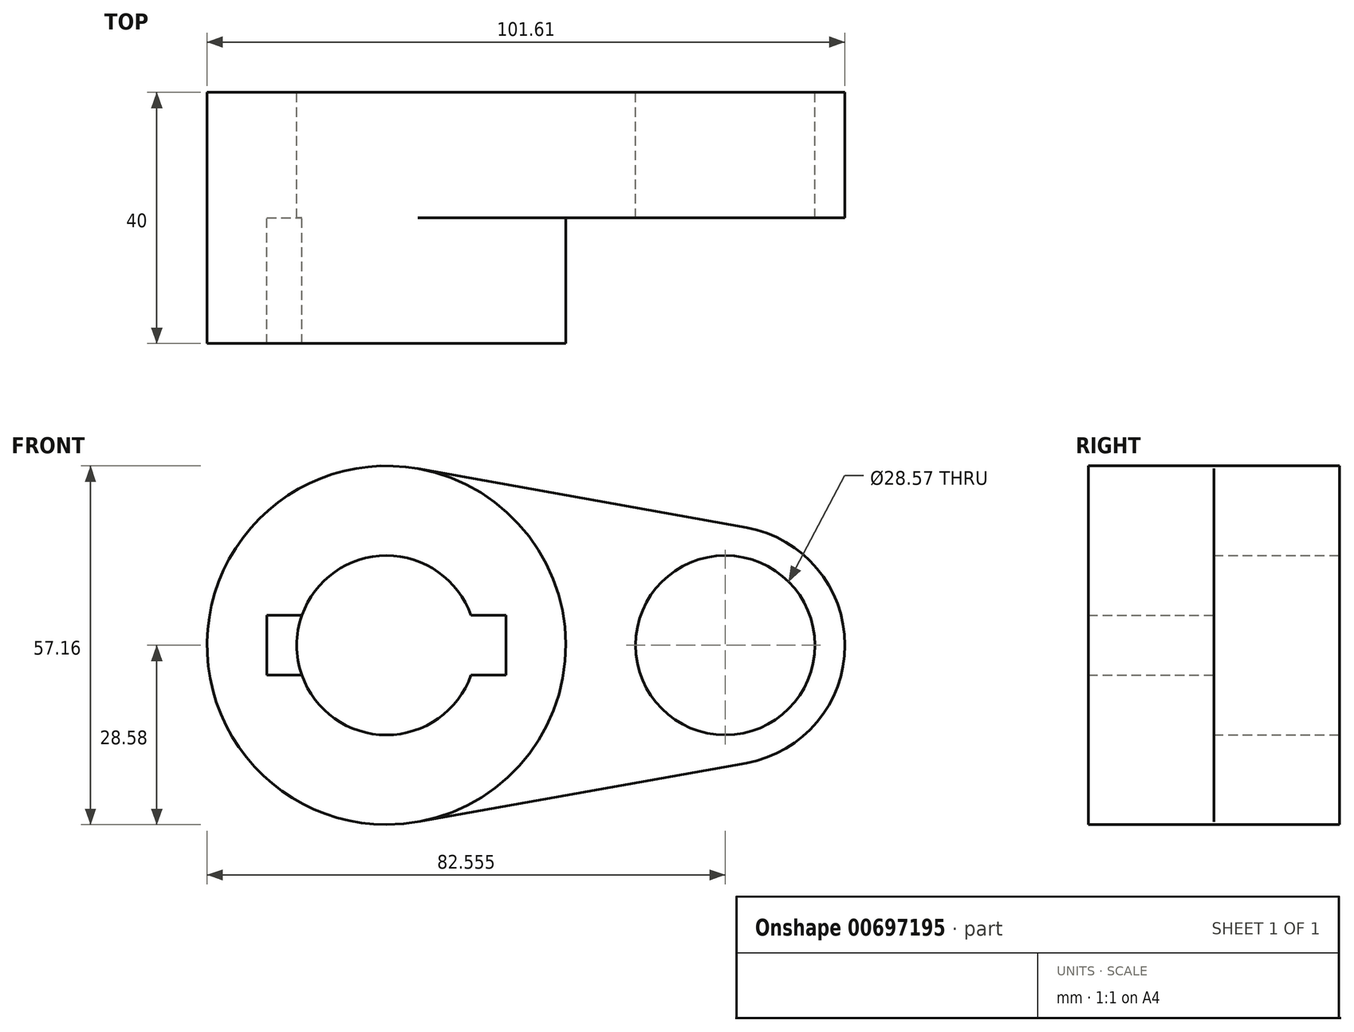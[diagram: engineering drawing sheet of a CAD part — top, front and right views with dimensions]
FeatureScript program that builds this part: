
annotation { "Feature Type Name" : "Feature", "Feature Type Description" : "" }
export const myFeature = defineFeature(function(context is Context, id is Id, definition is map)
    precondition{}
    {
        {
            var Q0;
            Q0=qCreatedBy(makeId("Front.planeOp"),FACE);
            var sketch = newSketch(context, id + "F0", { "sketchPlane" : qUnion([Q0])});
            skCircle(sketch, "E0", {"center": v(0, 0) * mm, "radius": 28.58 * mm});
            skCircle(sketch, "E1", {"center": v(53.98, 0) * mm, "radius": 19.05 * mm});
            skCircle(sketch, "E2", {"center": v(0, 0) * mm, "radius": 14.29 * mm});
            skCircle(sketch, "E3", {"center": v(53.98, 0) * mm, "radius": 14.29 * mm});
            skLineSegment(sketch, "E4.bottom", {"start": v(19.05, -4.76) * mm, "end": v(-19.05, -4.76) * mm});
            skLineSegment(sketch, "E4.top", {"start": v(19.05, 4.76) * mm, "end": v(-19.05, 4.76) * mm});
            skLineSegment(sketch, "E4.left", {"start": v(19.05, -4.76) * mm, "end": v(19.05, 4.76) * mm});
            skLineSegment(sketch, "E4.right", {"start": v(-19.05, -4.76) * mm, "end": v(-19.05, 4.76) * mm});
            skLineSegment(sketch, "E5", {"start": v(57.34, 18.75) * mm, "end": v(5.04, 28.13) * mm});
            skLineSegment(sketch, "E6", {"start": v(57.34, -18.75) * mm, "end": v(5.04, -28.13) * mm});
            skSolve(sketch);
        }
        {
            var Q0;
            {var subQ0=sQuery(id+"F0.wireOp",EDGE,"E5");Q0=makeQuery(id+"F0.imprint","IMPRINT",FACE,{"disambiguationData":[TD([[makeQuery(id+"F0.imprint","IMPRINT",EDGE,{"derivedFrom":subQ0}),1.0]])]});}
            var Q1;
            Q1=makeQuery(id+"F0.imprint","IMPRINT",FACE,{"disambiguationData":[TD([[makeQuery(id+"F0.imprint","IMPRINT",EDGE,{"derivedFrom":sQuery(id+"F0.wireOp",EDGE,"E3")}),-1.0]])]});
            var Q2;
            {var subQ4=sQuery(id+"F0.wireOp",EDGE,"E4.left");Q2=makeQuery(id+"F0.imprint","IMPRINT",FACE,{"disambiguationData":[TD([[makeQuery(id+"F0.imprint","IMPRINT",EDGE,{"derivedFrom":subQ4}),-1.0]])]});}
            var Q3;
            {var subQ5=sQuery(id+"F0.wireOp",EDGE,"E4.right");Q3=makeQuery(id+"F0.imprint","IMPRINT",FACE,{"disambiguationData":[TD([[makeQuery(id+"F0.imprint","IMPRINT",EDGE,{"derivedFrom":subQ5}),-1.0]])]});}
            extrude(context, id + "F1", {"entities" : qUnion([Q0, Q1, Q2, Q3]), "depth" : 20 * mm, "offsetDistance" : 25.4 * mm});
        }
        {
            var Q0;
            {var subQ4=sQuery(id+"F0.wireOp",EDGE,"E4.left");Q0=makeQuery(id+"F0.imprint","IMPRINT",FACE,{"disambiguationData":[TD([[makeQuery(id+"F0.imprint","IMPRINT",EDGE,{"derivedFrom":subQ4}),-1.0]])]});}
            extrude(context, id + "F2", {"entities" : qUnion([Q0]), "operationType" : NewBodyOperationType.ADD, "depth" : 40 * mm, "offsetDistance" : 25 * mm});
        }
    });
